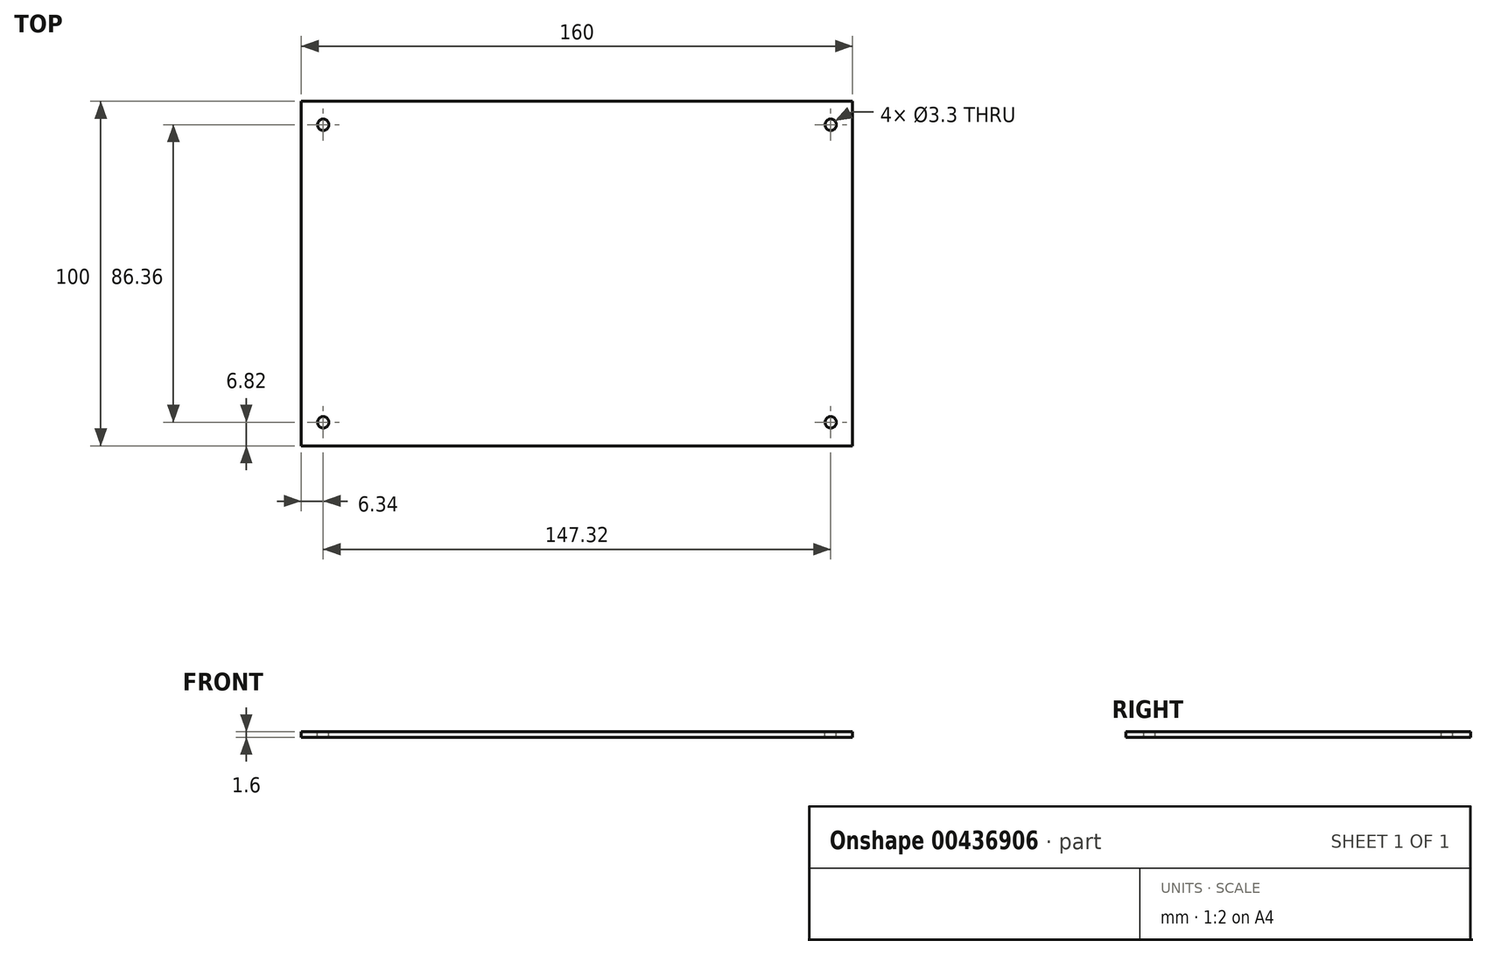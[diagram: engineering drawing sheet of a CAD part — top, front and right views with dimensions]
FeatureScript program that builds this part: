
annotation { "Feature Type Name" : "Feature", "Feature Type Description" : "" }
export const myFeature = defineFeature(function(context is Context, id is Id, definition is map)
    precondition{}
    {
        {
            var Q0;
            Q0=qCreatedBy(makeId("Top.planeOp"),FACE);
            var sketch = newSketch(context, id + "F0", { "sketchPlane" : qUnion([Q0])});
            skLineSegment(sketch, "E0.bottom", {"start": v(0, 0) * mm, "end": v(160, 0) * mm});
            skLineSegment(sketch, "E0.top", {"start": v(0, 100) * mm, "end": v(160, 100) * mm});
            skLineSegment(sketch, "E0.left", {"start": v(0, 0) * mm, "end": v(0, 100) * mm});
            skLineSegment(sketch, "E0.right", {"start": v(160, 0) * mm, "end": v(160, 100) * mm});
            skSolve(sketch);
        }
        {
            var Q0;
            Q0=qSketchRegion(id+"F0",true);
            extrude(context, id + "F1", {"entities" : qUnion([Q0]), "depth" : 1.6 * mm});
        }
        {
            var Q0;
            Q0=makeQuery(id+"F1.opExtrude","CAP_FACE",FACE,{"disambiguationData":[OSD([sQuery(id+"F0.wireOp",EDGE,"E0.bottom"),sQuery(id+"F0.wireOp",EDGE,"E0.top"),sQuery(id+"F0.wireOp",EDGE,"E0.left"),sQuery(id+"F0.wireOp",EDGE,"E0.right")])],"isStart":false});
            var sketch = newSketch(context, id + "F2", { "sketchPlane" : qUnion([Q0])});
            skPoint(sketch, "E1", {"position": v(6.34, 6.82) * mm});
            skPoint(sketch, "E2.0.1.0", {"position": v(6.34, 93.18) * mm});
            skPoint(sketch, "E2.1.0.0", {"position": v(153.66, 6.82) * mm});
            skPoint(sketch, "E2.1.1.0", {"position": v(153.66, 93.18) * mm});
            skLineSegment(sketch, "E2.direction1", {"start": v(6.34, 6.82) * mm, "end": v(153.66, 6.82) * mm, "construction": true});
            skLineSegment(sketch, "E2.direction2", {"start": v(6.34, 6.82) * mm, "end": v(6.34, 93.18) * mm, "construction": true});
            skSolve(sketch);
        }
        {
            var Q0;
            Q0=sQuery(id+"F2.wireOp",VERTEX,"E2.0.1.0");
            var Q1;
            Q1=sQuery(id+"F2.wireOp",VERTEX,"E1");
            var Q2;
            Q2=sQuery(id+"F2.wireOp",VERTEX,"E2.1.0.0");
            var Q3;
            Q3=sQuery(id+"F2.wireOp",VERTEX,"E2.1.1.0");
            var Q4;
            Q4=makeQuery(id+"F1.opExtrude","SWEPT_BODY",BODY,{"disambiguationData":[OSD([sQuery(id+"F0.wireOp",EDGE,"E0.bottom"),sQuery(id+"F0.wireOp",EDGE,"E0.top"),sQuery(id+"F0.wireOp",EDGE,"E0.left"),sQuery(id+"F0.wireOp",EDGE,"E0.right")])]});
            hole(context, id + "F3", {"style" : HoleStyle.SIMPLE, "endStyle" : HoleEndStyle.THROUGH, "standardTappedOrClearance" : lookupTablePath({ "standard" : "ISO", "fit" : "Normal", "size" : "M3", "type" : "Clearance" }), "standardBlindInLast" : lookupTablePath({ "fit" : "Standard", "standard" : "ISO", "size" : "M3", "type" : "Clearance" }), "holeDiameter" : 3.3 * mm, "isTappedThrough" : true, "tappedDepth" : 12 * mm, "tapClearance" : 3, "locations" : qUnion([Q0, Q1, Q2, Q3]), "scope" : qUnion([Q4])});
        }
    });
